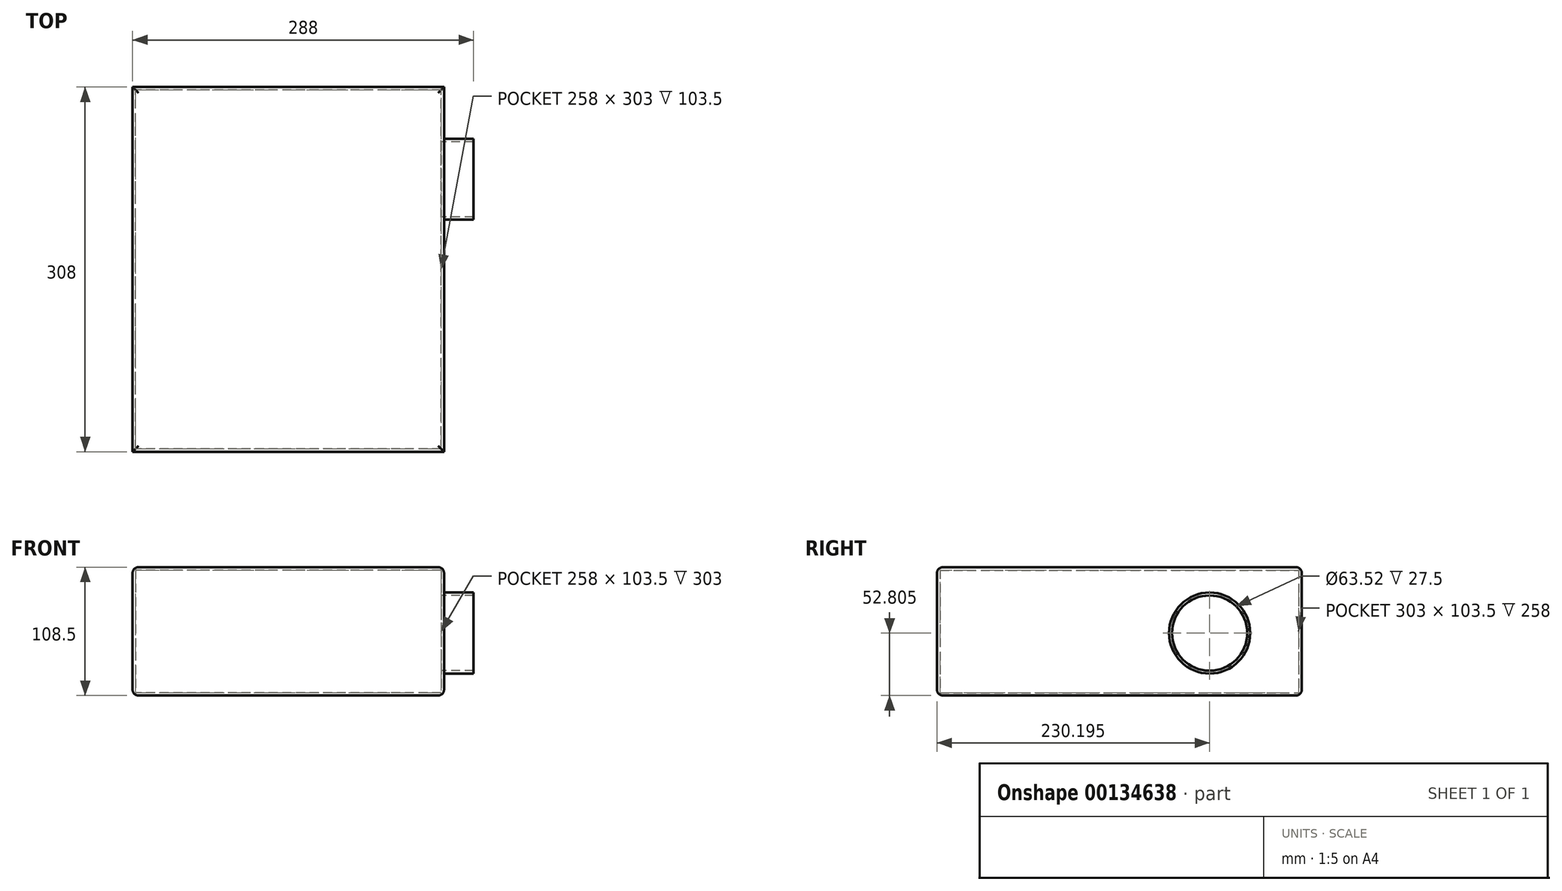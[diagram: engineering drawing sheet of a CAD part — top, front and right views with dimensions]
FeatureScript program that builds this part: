
annotation { "Feature Type Name" : "Feature", "Feature Type Description" : "" }
export const myFeature = defineFeature(function(context is Context, id is Id, definition is map)
    precondition{}
    {
        {
            var Q0;
            Q0=qCreatedBy(makeId("Top.planeOp"),FACE);
            var sketch = newSketch(context, id + "F0", { "sketchPlane" : qUnion([Q0])});
            skLineSegment(sketch, "E0.bottom", {"start": v(131.5, -154) * mm, "end": v(-131.5, -154) * mm});
            skLineSegment(sketch, "E0.top", {"start": v(131.5, 154) * mm, "end": v(-131.5, 154) * mm});
            skLineSegment(sketch, "E0.left", {"start": v(131.5, -154) * mm, "end": v(131.5, 154) * mm});
            skLineSegment(sketch, "E0.right", {"start": v(-131.5, -154) * mm, "end": v(-131.5, 154) * mm});
            skPoint(sketch, "E0.middle", {"position": v(0, 0) * mm});
            skSolve(sketch);
        }
        {
            var Q0;
            Q0=makeQuery(id+"F0.imprint","IMPRINT",FACE,{"disambiguationData":[TD([[makeQuery(id+"F0.imprint","IMPRINT",EDGE,{"derivedFrom":sQuery(id+"F0.wireOp",EDGE,"E0.bottom")}),-1.0]])]});
            extrude(context, id + "F1", {"entities" : qUnion([Q0]), "depth" : 108.5 * mm});
        }
        {
            var Q0;
            Q0=makeQuery(id+"F1.opExtrude","SWEPT_FACE",FACE,{"disambiguationData":[OSD([sQuery(id+"F0.wireOp",EDGE,"E0.left")])]});
            var sketch = newSketch(context, id + "F2", { "sketchPlane" : qUnion([Q0])});
            skCircle(sketch, "E1", {"center": v(76.2, 52.8) * mm, "radius": 34.26 * mm});
            skSolve(sketch);
        }
        {
            var Q0;
            Q0=makeQuery(id+"F2.imprint","IMPRINT",FACE,{"disambiguationData":[TD([[makeQuery(id+"F2.imprint","IMPRINT",EDGE,{"derivedFrom":sQuery(id+"F2.wireOp",EDGE,"E1")}),1.0]])]});
            extrude(context, id + "F3", {"entities" : qUnion([Q0]), "operationType" : NewBodyOperationType.ADD, "depth" : 25 * mm});
        }
        {
            var Q0;
            Q0=makeQuery(id+"F3.opExtrude","CAP_FACE",FACE,{"disambiguationData":[OSD([sQuery(id+"F2.wireOp",EDGE,"E1")])],"isStart":false});
            shell(context, id + "F4", {"entities" : qUnion([Q0]), "thickness" : 2.5 * mm});
        }
        {
            var Q0;
            Q0=makeQuery(id+"F1.opExtrude","CAP_EDGE",EDGE,{"disambiguationData":[OSD([sQuery(id+"F0.wireOp",EDGE,"E0.top")])],"isStart":false});
            var Q1;
            Q1=makeQuery(id+"F1.opExtrude","CAP_EDGE",EDGE,{"disambiguationData":[OSD([sQuery(id+"F0.wireOp",EDGE,"E0.bottom")])],"isStart":false});
            var Q2;
            Q2=makeQuery(id+"F1.opExtrude","CAP_EDGE",EDGE,{"disambiguationData":[OSD([sQuery(id+"F0.wireOp",EDGE,"E0.top")])],"isStart":true});
            var Q3;
            Q3=makeQuery(id+"F1.opExtrude","CAP_EDGE",EDGE,{"disambiguationData":[OSD([sQuery(id+"F0.wireOp",EDGE,"E0.bottom")])],"isStart":true});
            var Q4;
            Q4=makeQuery(id+"F1.opExtrude","CAP_EDGE",EDGE,{"disambiguationData":[OSD([sQuery(id+"F0.wireOp",EDGE,"E0.left")])],"isStart":false});
            var Q5;
            Q5=makeQuery(id+"F1.opExtrude","CAP_EDGE",EDGE,{"disambiguationData":[OSD([sQuery(id+"F0.wireOp",EDGE,"E0.left")])],"isStart":true});
            var Q6;
            Q6=makeQuery(id+"F1.opExtrude","CAP_EDGE",EDGE,{"disambiguationData":[OSD([sQuery(id+"F0.wireOp",EDGE,"E0.right")])],"isStart":false});
            var Q7;
            Q7=makeQuery(id+"F1.opExtrude","CAP_EDGE",EDGE,{"disambiguationData":[OSD([sQuery(id+"F0.wireOp",EDGE,"E0.right")])],"isStart":true});
            fillet(context, id + "F5", {"entities" : qUnion([Q0, Q1, Q2, Q3, Q4, Q5, Q6, Q7]), "radius" : 5 * mm, "tangentPropagation" : true, "allowEdgeOverflow" : false});
        }
    });
